# Revit family: Genelec_4430
name_source: partatom
category: Generic Models
units: mm (PartAtom-declared; Revit-internal decimal feet)

## family parameters
Always vertical = No
Can host rebar = No
Cut with Voids When Loaded = No
Maintain Annotation Orientation = No
Part Type = Normal
Room Calculation Point = Yes
Round Connector Dimension = Use Diameter
Shared = No
Work Plane-Based = No

## types (2) — shared parameters
Accuracy of Frequency Response = ± 1.5 dB (58 Hz - 20 kHz)
Acoustic Axis = 175
BIMobject category = Audio Electronics
Color = RAL_9018_Papyrus White
Connections = 1 x RJ45 for PoE power, management and audio in AES67 / Dante format
1 x Euroblock Analog Input
Default Elevation = 1200 mm
Depth = 178 mm
Description = The exeptional 4430A Smart IP Active PoE-Powered Installation Loudspeaker combines class-leading sound quality with single cable convenience, using PoE to produce uncompromised SPL and acoustic performance.
Dispersion Angle = H 120° V 100°
Driver Dimensions = ⌀ 130 mm Woofer + ⌀ 19 mm Tweeter
Export Type to IFC As = IfcAudioVisualApplianceType
Finish Type = Die cast aluminium
Frequency Response = 45 Hz - 39 kHz (-6 dB)
Height = 285 mm
IFC Classification = Electric Appliance
IFC Name = 4430A
Line Drawing = https://assets.ctfassets.net
Mains Voltage = PoE+/PoE
Manufacturer = GENELEC
Manufacturer Country = Finland
Max. short term sine wave acoustic output  on axis in half space, averaged from 100Hz to 3 kHz = ≥ 104 dB SPL
Maximum long term RMS acoustic output in same conditions with IEC weighted noise (limited by driver unit protection circuit) = ≥ 96 dB SPL
Model = 4430
Model Description = Smart IP Installation Speaker
Model Name = 4430A
Mounting Type = Includes mount: 4000-410B/W
Power Consumption = 26 W
Power consumption Idle = ≤5 W
Power consumption Standby = ≤4 W (ISS Active)
Price List Description = Recycled-aluminium cabinet with tightly controlled directivity and minimum diffraction for excellent clarity and intelligibility. Both drivers have metal protection grilles, with 130 mm (5 in) LF and 19 mm (3/4 in) HF transducers. Integrated crossover and Class D amplifiers 50 W + 50 W. Max. SPL 104 dB, frequency response 45 Hz - 39 kHz (-6 dB). Control by Smart IP Manager software, including device discovery, room equalisation, system organisation and status monitoring. On-Off switch on the rear panel. Dimensions: H 285 x W 189 x D 178 mm, weight 5.1 kg.
Product Family = Installation Speaker
Product Group = 4000 Series Installation Speakers
Self-generated Noise = ≤5 dB
Type IFC Predefined Type = SPEAKER
Type Image = <None>
URL = https://www.genelec.com
Uniclass 2.0 Description = Sound Amplifiers
Weight = 5.1
Width = 189 mm

## per-type parameters (varying)
| type | Horizontal | Vertical |
| 4430 Vertical | No | Yes |
| 4430 Horizontal | Yes | No |

## geometry (parser evidence)
native form markers: Blend x8
no freeform markers — native parametric forms only
